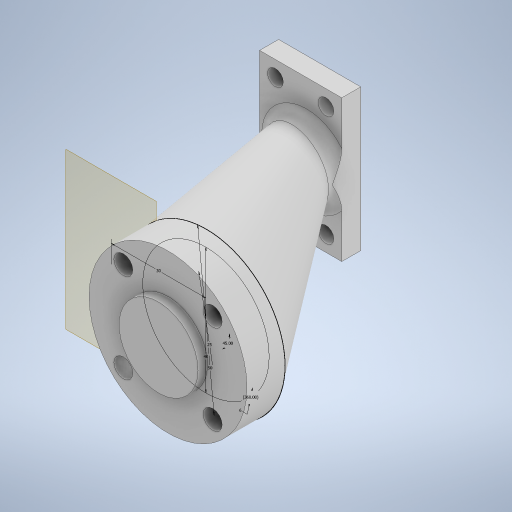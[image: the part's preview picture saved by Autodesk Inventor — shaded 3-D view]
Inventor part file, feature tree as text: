
AUTODESK INVENTOR PART (.ipt)
format: ipt  version: 2024.3 (Build 283343000, 343)  size: 333,824 bytes
history: native  units: mm
features: extrude x3, sketch x3, other x3, plane x1, loft x1, fillet x1, reference x1
ambient origin geometry x8: Origin, YZ Plane, XZ Plane, XY Plane, X Axis, Y Axis, Z Axis, Center Point
bodies: Solid1 (feature_tree)
feature tree (13):
  extrude  "Extrusion1"  Depth=17.5mm
  sketch  "Sketch2"  dims[d3=5.0mm d4=6.0mm d5=0.0mm]
  plane  "Work Plane1"
  sketch  "Sketch3"  dims[d6=20.0mm d7=60.0mm d8=30.0mm d10=50.0mm d11=40.0mm d12=45.0deg d13=6.0mm d14=40.0mm d16=360.0deg d18=25.0mm d19=12.0mm d20=0.0mm d21=15.0mm d22=0.0mm d23=0.0mm d24=90.0deg d25=0.0mm d26=90.0deg d27=3.0mm]
  extrude  "Extrusion2"  Depth=6.0mm TaperAngle=0.0deg
  extrude  "Extrusion3"  Depth=60.0mm
  loft  "Loft1"
  fillet  "Fillet1"  Radius=50.0mm
  sketch  "Sketch1"  dims[d1=8.0mm d2=17.5mm]
  reference  "Reference1"
  other  "<userpath>\Desktop\Unal\Robotica\proyecto\garra neumatica\Assembly1.iam"
  other  "Assembly1.iam"
  other  "housing:1"
